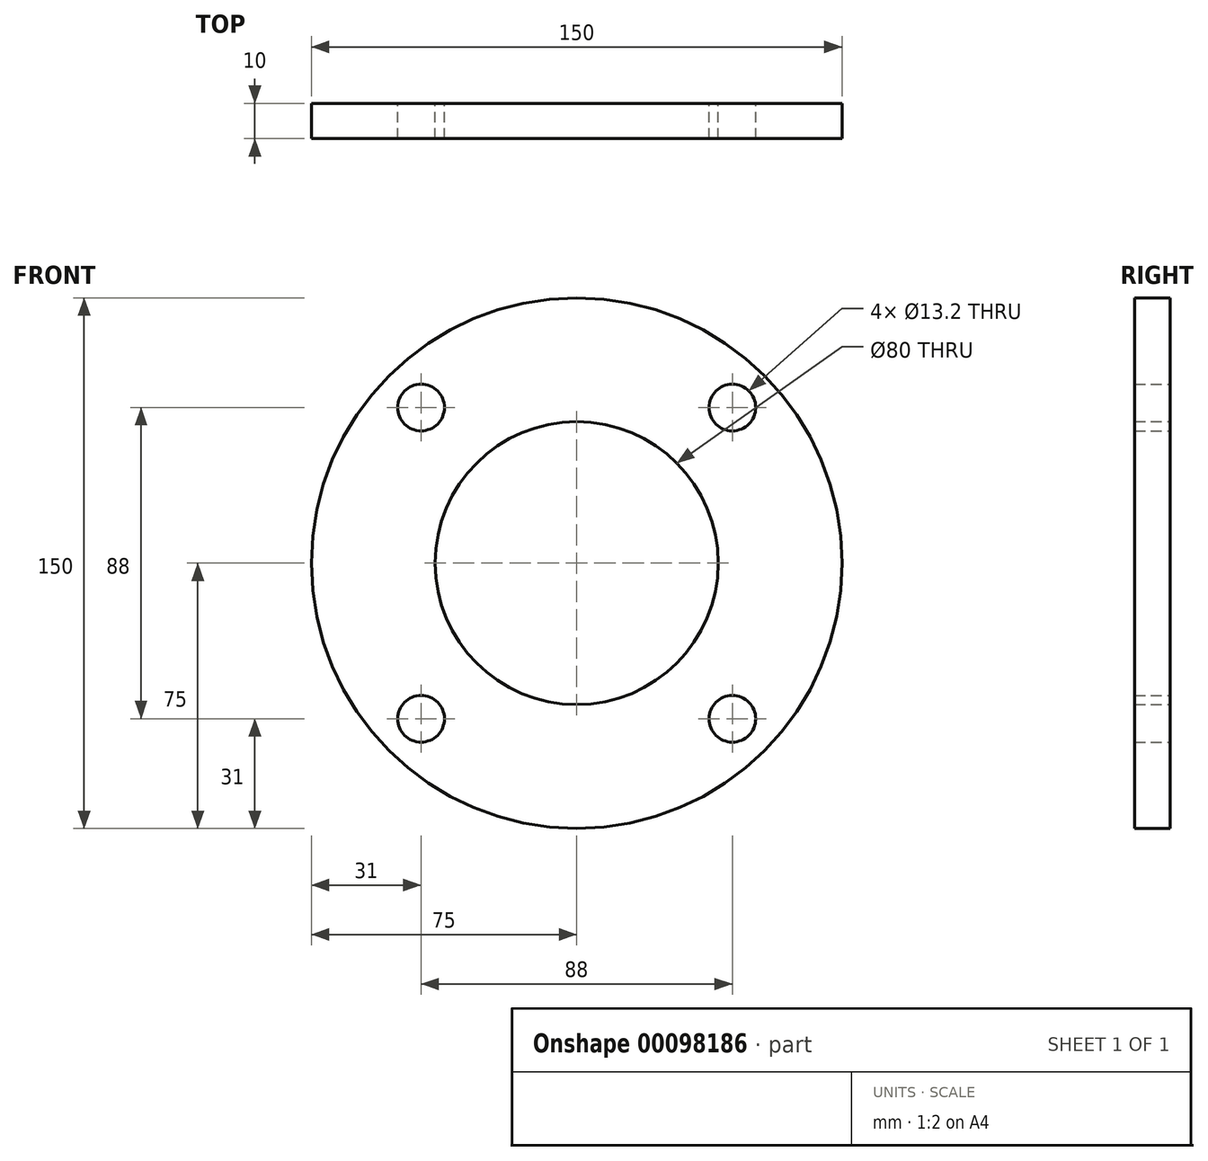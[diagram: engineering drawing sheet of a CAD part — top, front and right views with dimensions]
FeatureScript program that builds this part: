
annotation { "Feature Type Name" : "Feature", "Feature Type Description" : "" }
export const myFeature = defineFeature(function(context is Context, id is Id, definition is map)
    precondition{}
    {
        {
            var Q0;
            Q0=qCreatedBy(makeId("Front.planeOp"),FACE);
            var sketch = newSketch(context, id + "F0", { "sketchPlane" : qUnion([Q0])});
            skCircle(sketch, "E0", {"center": v(0, 0) * mm, "radius": 40 * mm});
            skCircle(sketch, "E1", {"center": v(0, 0) * mm, "radius": 75 * mm});
            skLineSegment(sketch, "E2", {"start": v(0, 0) * mm, "end": v(0, 44) * mm});
            skLineSegment(sketch, "E3", {"start": v(0, 44) * mm, "end": v(44, 44) * mm});
            skLineSegment(sketch, "E4", {"start": v(44, 44) * mm, "end": v(44, -44) * mm});
            skLineSegment(sketch, "E5", {"start": v(44, -44) * mm, "end": v(-44, -44) * mm});
            skLineSegment(sketch, "E6", {"start": v(-44, -44) * mm, "end": v(-44, 44) * mm});
            skSolve(sketch);
        }
        {
            var Q0;
            Q0=makeQuery(id+"F0.imprint","IMPRINT",FACE,{"disambiguationData":[TD([[makeQuery(id+"F0.imprint","IMPRINT",EDGE,{"derivedFrom":sQuery(id+"F0.wireOp",EDGE,"E0")}),-1.0]])]});
            extrude(context, id + "F1", {"entities" : qUnion([Q0]), "depth" : 10 * mm, "offsetDistance" : 25 * mm});
        }
        {
            var Q0;
            Q0=makeQuery(id+"F1.opExtrude","CAP_FACE",FACE,{"disambiguationData":[OSD([sQuery(id+"F0.wireOp",EDGE,"E0"),sQuery(id+"F0.wireOp",EDGE,"E1")])],"isStart":false});
            var sketch = newSketch(context, id + "F2", { "sketchPlane" : qUnion([Q0])});
            skLineSegment(sketch, "E7", {"start": v(0, 0) * mm, "end": v(0, 44) * mm});
            skLineSegment(sketch, "E8", {"start": v(0, 44) * mm, "end": v(44, 44) * mm});
            skLineSegment(sketch, "E9", {"start": v(44, 44) * mm, "end": v(44, -44) * mm});
            skLineSegment(sketch, "E10", {"start": v(44, -44) * mm, "end": v(-44, -44) * mm});
            skLineSegment(sketch, "E11", {"start": v(-44, -44) * mm, "end": v(-44, 44) * mm});
            skPoint(sketch, "E12", {"position": v(-44, 44) * mm});
            skPoint(sketch, "E13", {"position": v(-44, -44) * mm});
            skPoint(sketch, "E14", {"position": v(44, -44) * mm});
            skPoint(sketch, "E15", {"position": v(44, 44) * mm});
            skSolve(sketch);
        }
        {
            var Q0;
            Q0=sQuery(id+"F2.wireOp",VERTEX,"E12");
            var Q1;
            Q1=sQuery(id+"F2.wireOp",VERTEX,"E13");
            var Q2;
            Q2=sQuery(id+"F2.wireOp",VERTEX,"E14");
            var Q3;
            Q3=sQuery(id+"F2.wireOp",VERTEX,"E15");
            var Q4;
            Q4=makeQuery(id+"F1.opExtrude","SWEPT_BODY",BODY,{"disambiguationData":[OSD([sQuery(id+"F0.wireOp",EDGE,"E0"),sQuery(id+"F0.wireOp",EDGE,"E1")])]});
            hole(context, id + "F3", {"style" : HoleStyle.SIMPLE, "endStyle" : HoleEndStyle.THROUGH, "standardTappedOrClearance" : lookupTablePath({ "standard" : "ISO", "fit" : "Normal", "size" : "M12", "type" : "Clearance" }), "standardBlindInLast" : lookupTablePath({ "fit" : "Standard", "standard" : "ISO", "size" : "M12", "type" : "Clearance" }), "holeDiameter" : 13.2 * mm, "majorDiameter" : 5 * mm, "isTappedThrough" : true, "tappedDepth" : 12 * mm, "tapClearance" : 3, "locations" : qUnion([Q0, Q1, Q2, Q3]), "scope" : qUnion([Q4]), "startStyle" : HoleStartStyle.PART});
        }
    });
